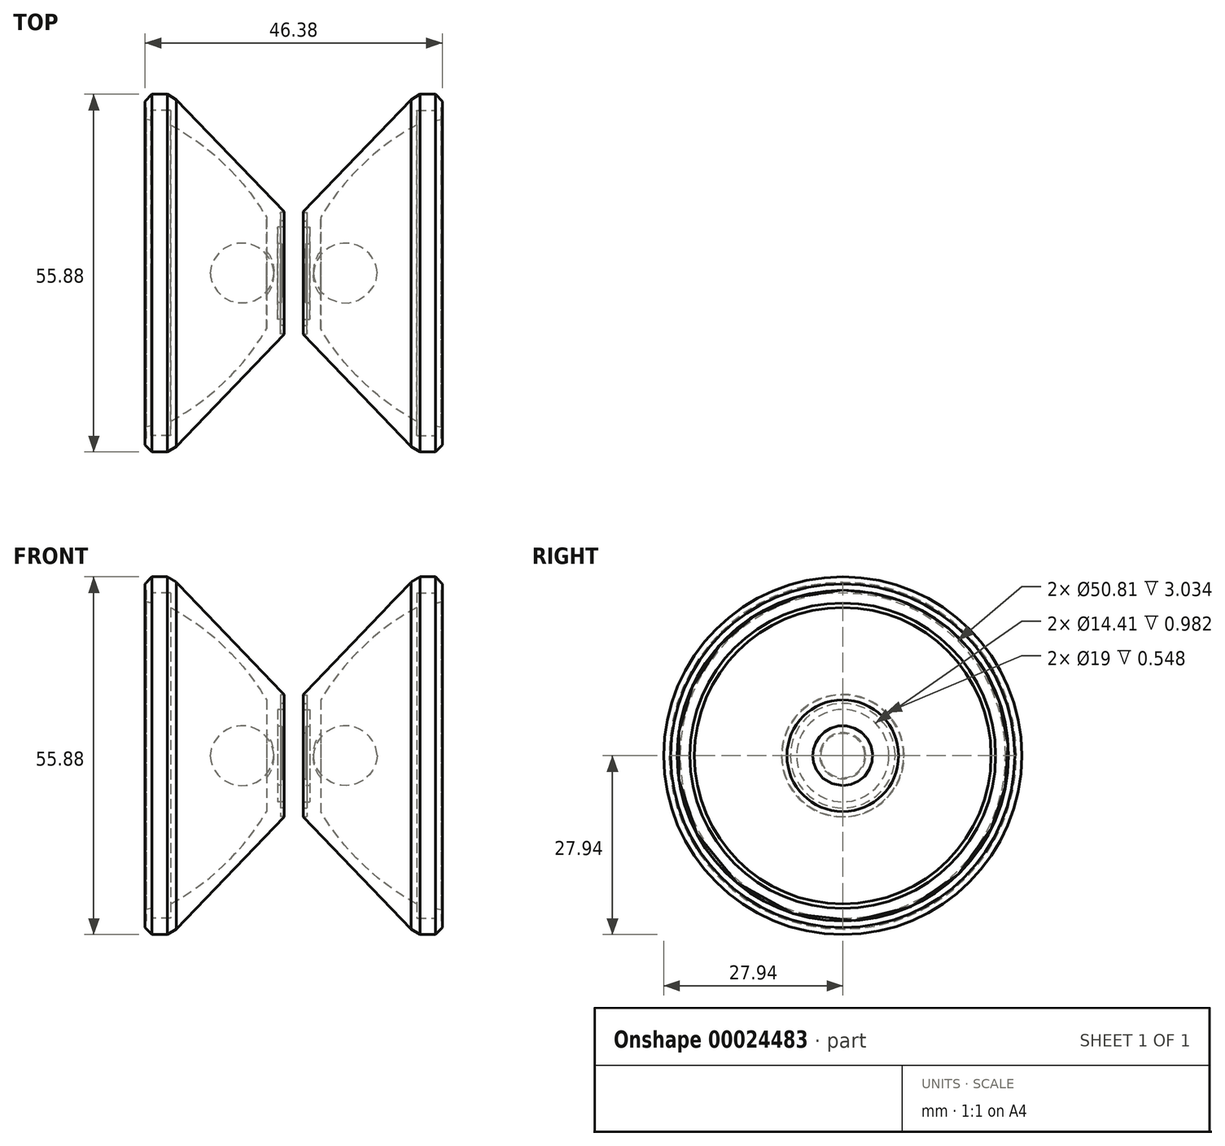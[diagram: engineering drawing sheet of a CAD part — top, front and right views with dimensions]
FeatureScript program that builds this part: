
annotation { "Feature Type Name" : "Feature", "Feature Type Description" : "" }
export const myFeature = defineFeature(function(context is Context, id is Id, definition is map)
    precondition{}
    {
        {
            var Q0;
            Q0=qCreatedBy(makeId("Front.planeOp"),FACE);
            var sketch = newSketch(context, id + "F0", { "sketchPlane" : qUnion([Q0])});
            skLineSegment(sketch, "E0", {"start": v(-11.06, 24.06) * mm, "end": v(-11.06, 25.84) * mm});
            skLineSegment(sketch, "E1", {"start": v(-11.22, 25.98) * mm, "end": v(-11.22, 26.84) * mm});
            skLineSegment(sketch, "E2", {"start": v(-11.22, 26.84) * mm, "end": v(-10.17, 27.94) * mm});
            skLineSegment(sketch, "E3", {"start": v(-10.17, 27.94) * mm, "end": v(-7.72, 27.94) * mm});
            skLineSegment(sketch, "E4", {"start": v(-7.72, 27.94) * mm, "end": v(-6.32, 27.09) * mm});
            skLineSegment(sketch, "E5", {"start": v(-6.32, 27.09) * mm, "end": v(10.47, 9.58) * mm});
            skLineSegment(sketch, "E6", {"start": v(10.47, 9.58) * mm, "end": v(10.47, 9.5) * mm});
            skLineSegment(sketch, "E7", {"start": v(10.47, 9.5) * mm, "end": v(9.92, 9.5) * mm});
            skLineSegment(sketch, "E8", {"start": v(9.92, 9.5) * mm, "end": v(9.92, 8.17) * mm});
            skLineSegment(sketch, "E9", {"start": v(9.92, 8.17) * mm, "end": v(10.47, 8.17) * mm});
            skLineSegment(sketch, "E10", {"start": v(10.47, 8.17) * mm, "end": v(10.47, 7.2) * mm});
            skLineSegment(sketch, "E11", {"start": v(10.47, 7.2) * mm, "end": v(9.49, 7.2) * mm});
            skLineSegment(sketch, "E12", {"start": v(9.49, 7.2) * mm, "end": v(9.49, 4.6) * mm});
            skLineSegment(sketch, "E13", {"start": v(9.49, 4.6) * mm, "end": v(10.09, 4.6) * mm});
            skArc(sketch, "E14", {"start": v(7.75, 8.71) * mm, "mid": v(1.23, 16.93) * mm, "end": v(-7.22, 23.15) * mm});
            skLineSegment(sketch, "E15", {"start": v(7.75, 8.71) * mm, "end": v(7.75, 3.46) * mm});
            skArc(sketch, "E16", {"start": v(8.87, 0) * mm, "mid": v(8.64, 1.83) * mm, "end": v(7.75, 3.46) * mm});
            skLineSegment(sketch, "E17", {"start": v(8.87, 0) * mm, "end": v(10.47, 0) * mm});
            skLineSegment(sketch, "E18", {"start": v(10.47, 0) * mm, "end": v(10.47, 3.6) * mm});
            skLineSegment(sketch, "E19", {"start": v(10.47, 3.6) * mm, "end": v(10.09, 3.6) * mm});
            skLineSegment(sketch, "E20", {"start": v(10.09, 3.6) * mm, "end": v(10.09, 4.6) * mm});
            skLineSegment(sketch, "E21", {"start": v(-7.22, 23.15) * mm, "end": v(-7.22, 25.4) * mm});
            skLineSegment(sketch, "E22", {"start": v(-7.22, 25.4) * mm, "end": v(-10.26, 25.4) * mm});
            skLineSegment(sketch, "E23", {"start": v(-10.26, 25.4) * mm, "end": v(-10.26, 23.85) * mm});
            skLineSegment(sketch, "E24", {"start": v(-10.26, 23.85) * mm, "end": v(-11.03, 24.02) * mm});
            skArc(sketch, "E25", {"start": v(-11.22, 25.98) * mm, "mid": v(-11.17, 25.87) * mm, "end": v(-11.06, 25.84) * mm});
            skPoint(sketch, "E26.visualSharp", {"position": v(-11.06, 24.03) * mm});
            skArc(sketch, "E26.filletArc", {"start": v(-11.06, 24.06) * mm, "mid": v(-11.05, 24.03) * mm, "end": v(-11.03, 24.02) * mm});
            skSolve(sketch);
        }
        {
            var Q0;
            Q0 = qSketchRegion(id + "F0", true);
            var Q1;
            Q1=sQuery(id+"F0.wireOp",EDGE,"E17");
            revolve(context, id + "F1", {"entities" : qUnion([Q0]), "axis" : qUnion([Q1]), "revolveType" : RevolveType.FULL});
        }
        {
            var Q0;
            Q0=makeQuery(id+"F1.opRevolve","SWEPT_FACE",FACE,{"disambiguationData":[OSD([sQuery(id+"F0.wireOp",EDGE,"E18")])]});
            cPlane(context, id + "F2", {"entities" : qUnion([Q0]), "cplaneType" : CPlaneType.OFFSET, "offset" : 1.5 * mm, "width" : 152.4 * mm, "height" : 152.4 * mm});
        }
        {
            var Q0;
            Q0=makeQuery(id+"F1.opRevolve","SWEPT_BODY",BODY,{"disambiguationData":[OSD([sQuery(id+"F0.wireOp",EDGE,"b0b98ef7-041b-48d8-8698-6f07fc21b9c6"),sQuery(id+"F0.wireOp",EDGE,"E0"),sQuery(id+"F0.wireOp",EDGE,"859e541a-2d4a-4d0c-8e06-e6897e5a8c52"),sQuery(id+"F0.wireOp",EDGE,"E1"),sQuery(id+"F0.wireOp",EDGE,"E2"),sQuery(id+"F0.wireOp",EDGE,"E3"),sQuery(id+"F0.wireOp",EDGE,"E4"),sQuery(id+"F0.wireOp",EDGE,"E5"),sQuery(id+"F0.wireOp",EDGE,"E6"),sQuery(id+"F0.wireOp",EDGE,"E7"),sQuery(id+"F0.wireOp",EDGE,"E8"),sQuery(id+"F0.wireOp",EDGE,"E9"),sQuery(id+"F0.wireOp",EDGE,"E10"),sQuery(id+"F0.wireOp",EDGE,"E11"),sQuery(id+"F0.wireOp",EDGE,"E12"),sQuery(id+"F0.wireOp",EDGE,"E13"),sQuery(id+"F0.wireOp",EDGE,"E14"),sQuery(id+"F0.wireOp",EDGE,"E15"),sQuery(id+"F0.wireOp",EDGE,"E16"),sQuery(id+"F0.wireOp",EDGE,"E17"),sQuery(id+"F0.wireOp",EDGE,"E18"),sQuery(id+"F0.wireOp",EDGE,"E19"),sQuery(id+"F0.wireOp",EDGE,"E20")])]});
            var Q1;
            Q1=qCreatedBy(id+"F2.planeOp",FACE);
            mirror(context, id + "F3", {"entities" : qUnion([Q0]), "mirrorPlane" : qUnion([Q1])});
        }
    });
